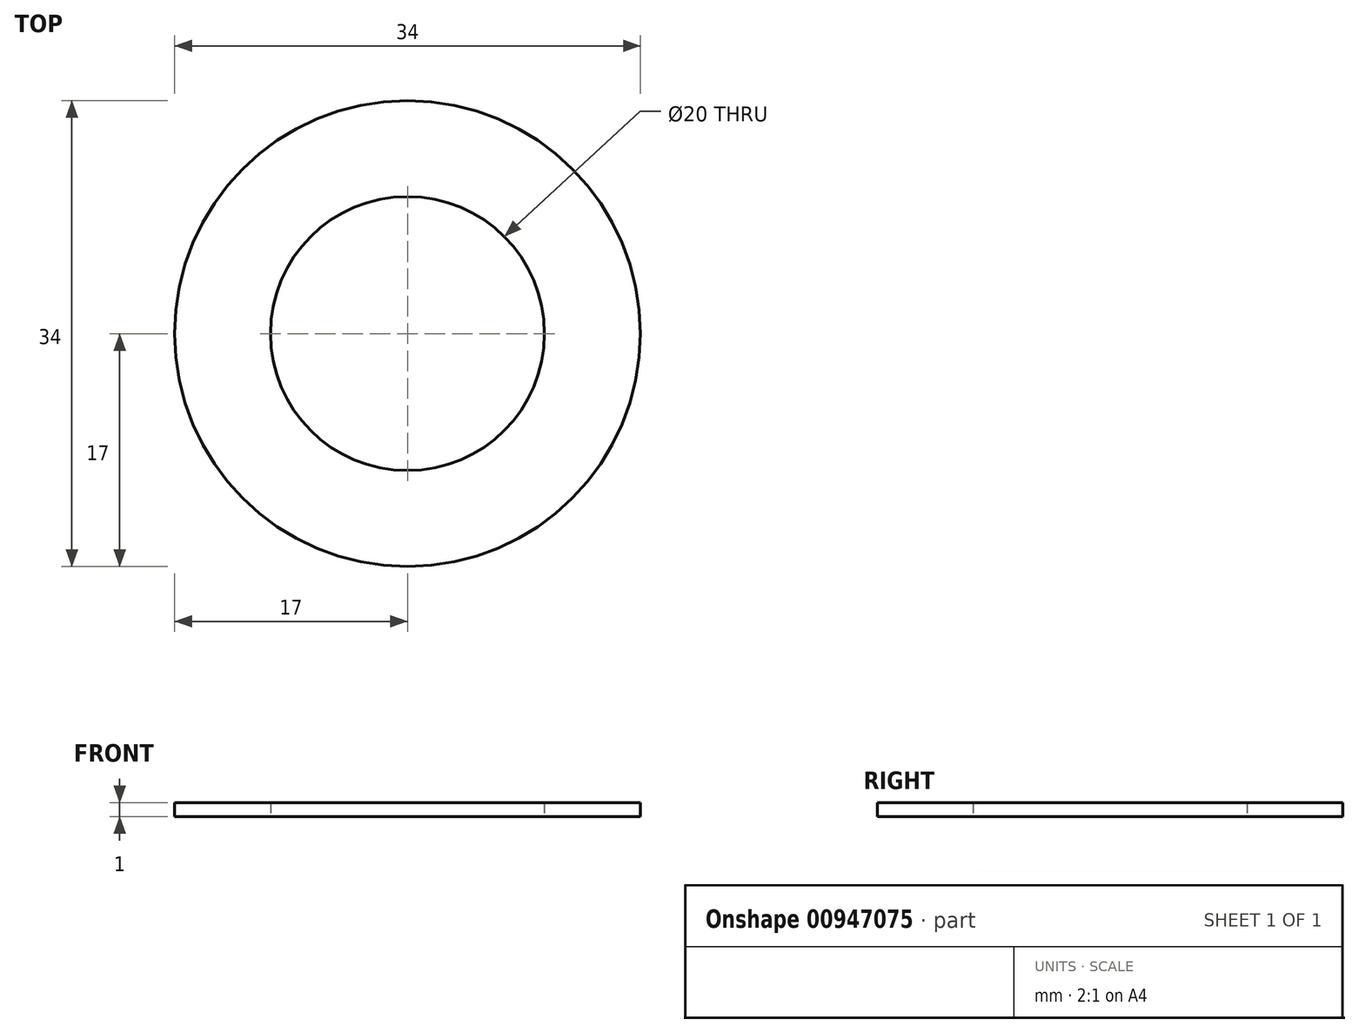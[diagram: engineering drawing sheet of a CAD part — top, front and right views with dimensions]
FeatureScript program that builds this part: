
annotation { "Feature Type Name" : "Feature", "Feature Type Description" : "" }
export const myFeature = defineFeature(function(context is Context, id is Id, definition is map)
    precondition{}
    {
        {
            var Q0;
            Q0=qCreatedBy(makeId("Top.planeOp"),FACE);
            var sketch = newSketch(context, id + "F0", { "sketchPlane" : qUnion([Q0])});
            skCircle(sketch, "E0", {"center": v(0, 0) * mm, "radius": 16.2 * mm});
            skCircle(sketch, "E1", {"center": v(0, 0) * mm, "radius": 17 * mm});
            skSolve(sketch);
        }
        {
            var Q0;
            Q0=makeQuery(id+"F0.imprint","IMPRINT",FACE,{"disambiguationData":[TD([[makeQuery(id+"F0.imprint","IMPRINT",EDGE,{"derivedFrom":sQuery(id+"F0.wireOp",EDGE,"nKFbHakR-xPsK-2WIt-yrDR-NFVg289ljqzI")}),1.0]])]});
            var Q1;
            Q1=makeQuery(id+"F0.imprint","IMPRINT",FACE,{"disambiguationData":[TD([[makeQuery(id+"F0.imprint","IMPRINT",EDGE,{"derivedFrom":sQuery(id+"F0.wireOp",EDGE,"E0")}),-1.0]])]});
            var Q2;
            Q2=makeQuery(id+"F0.imprint","IMPRINT",FACE,{"disambiguationData":[TD([[makeQuery(id+"F0.imprint","IMPRINT",EDGE,{"derivedFrom":sQuery(id+"F0.wireOp",EDGE,"E0")}),1.0]])]});
            extrude(context, id + "F1", {"entities" : qUnion([Q0, Q1, Q2]), "depth" : 1 * mm, "offsetDistance" : 25 * mm});
        }
        {
            var Q0;
            Q0=sQuery(id+"F0.wireOp",EDGE,"E0");
            extrude(context, id + "F2", {"bodyType" : ToolBodyType.SURFACE, "surfaceEntities" : qUnion([Q0]), "depth" : 3 * mm, "offsetDistance" : 25 * mm});
        }
        {
            var Q0;
            Q0=makeQuery(id+"F1.opExtrude","CAP_FACE",FACE,{"disambiguationData":[OSD([sQuery(id+"F0.wireOp",EDGE,"E1")])],"isStart":true});
            var sketch = newSketch(context, id + "F3", { "sketchPlane" : qUnion([Q0])});
            skCircle(sketch, "E2", {"center": v(0, 0) * mm, "radius": 10 * mm});
            skSolve(sketch);
        }
        {
            var Q0;
            Q0 = qSketchRegion(id + "F3", true);
            extrude(context, id + "F4", {"entities" : qUnion([Q0]), "operationType" : NewBodyOperationType.REMOVE, "oppositeDirection" : true, "depth" : 3 * mm, "offsetDistance" : 25 * mm});
        }
    });
